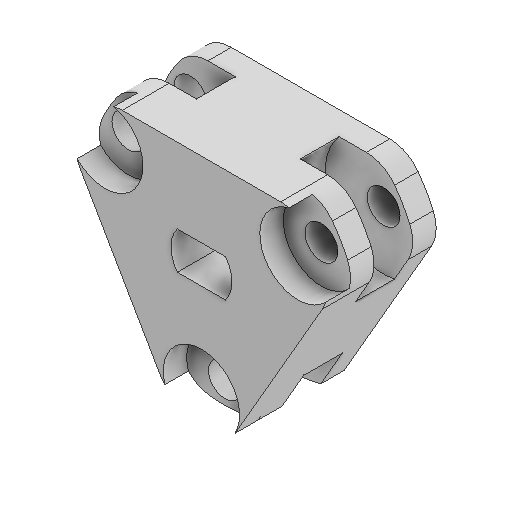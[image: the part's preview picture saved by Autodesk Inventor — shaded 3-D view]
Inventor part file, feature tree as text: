
AUTODESK INVENTOR PART (.ipt)
format: ipt  version: 2022 (Build 260153000, 153)  size: 284,672 bytes
history: native  units: mm
features: projected_geometry x7, sketch x5, extrude x4, hole x1, fillet x1
ambient origin geometry x8: Origin, YZ Plane, XZ Plane, XY Plane, X Axis, Y Axis, Z Axis, Center Point
bodies: Body1 (feature_tree)
feature tree (18):
  extrude  "Extrusion3"  Depth=9.5mm
  extrude  "Extrusion4"  Depth=2.8mm
  extrude  "Extrusion5"  Depth=5.2mm
  hole  "Bohrung1"  [1 undecoded]
  extrude  "Extrusion6"  Depth=10.0mm
  fillet  "Rundung1"  Radius=10.0mm
  sketch  "Skizze3"  dims[d10=22.8mm d11=9.5mm]
  sketch  "Skizze4"  dims[d12=2.8mm d13=2.8mm]
  projected_geometry  "Projizierte Kontur1"
  sketch  "Skizze6"  dims[d14=2.8mm d15=5.2mm]
  projected_geometry  "Projizierte Kontur2"
  projected_geometry  "Projizierte Kontur3"
  projected_geometry  "Projizierte Kontur4"
  projected_geometry  "Projizierte Kontur5"
  sketch  "Skizze7"  dims[d16=1.6mm d17=1.6mm]
  projected_geometry  "Projizierte Kontur6"
  sketch  "Skizze8"  dims[d18=4.0mm d19=0.0mm d20=10.0mm d21=10.0mm d22=10.0mm d23=3.3mm d24=0.0mm d25=2.0mm d26=0.0mm d27=2.8mm d28=6.0mm d29=6.5mm d30=2.0mm d31=90.0deg d32=15.0mm d33=20.594885mm d34=0.0mm d35=0.0mm d36=3.0mm]
  projected_geometry  "Projizierte Kontur7"
note: 1 required parameter value undecoded (feature->parameter linkage not recoverable at this tier; creation-order binding heuristic only, values carry confidence <= 0.55)
